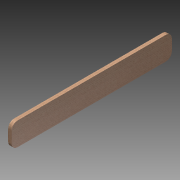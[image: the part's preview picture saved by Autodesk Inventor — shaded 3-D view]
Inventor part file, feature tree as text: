
AUTODESK INVENTOR PART (.ipt)
format: ipt  version: 2013 (Build 170138000, 138)  size: 89,088 bytes
history: native  units: in
note: dims shown in document units (in); Inventor stores cm internally (conversion verified against a paired STEP export)
features: extrude x1, fillet x1, sketch x1
ambient origin geometry x8: Origin, YZ Plane, XZ Plane, XY Plane, X Axis, Y Axis, Z Axis, Center Point
bodies: Solid1 (feature_tree)
feature tree (3):
  extrude  "Extrusion1"  Depth=0.75in
  fillet  "Fillet1"  Radius=34.625in
  sketch  "Sketch1"  dims[d0=5.0in d1=0.75in d2=34.625in d3=0.0in d4=1.3125in]
